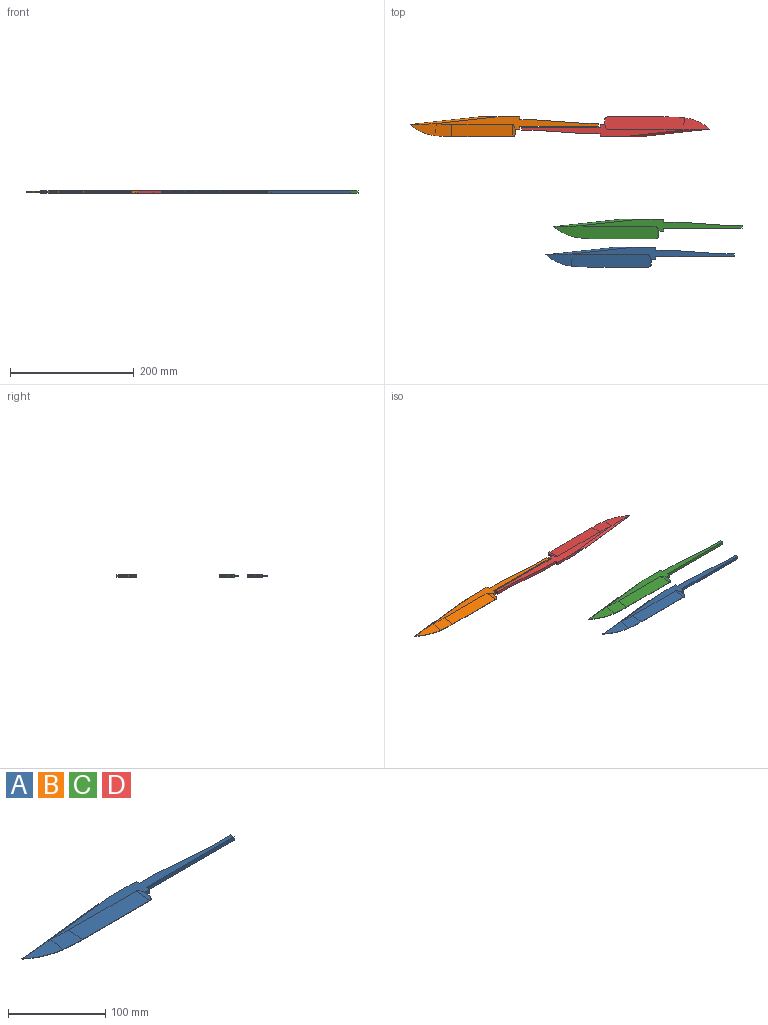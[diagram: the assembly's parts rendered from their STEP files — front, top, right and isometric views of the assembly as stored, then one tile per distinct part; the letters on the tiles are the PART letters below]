
ASSEMBLY  parts=4 mates=4
PART A: 27 faces, bbox 304.8x34.4x6.4 mm
  f0: cylinder r=4.65mm len=4.65mm, axis (0,0,-1), area 13.3mm2, adj f1,f4,f22,f26
  f1: plane 7.48x4.76mm, normal (1,0,0), area 29.5mm2, adj f0,f12,f22,f26
  f2: cylinder r=76.2mm len=40.9mm, axis (0,0,-1), area 23mm2, adj f3,f11,f17,f18,f21,f25
  f3: cylinder r=228.6mm len=26.84mm, axis (0,0,-1), area 13.7mm2, adj f2,f4,f20,f24
  f4: plane 97.93x0.51mm, normal (0,-1,0), area 49.7mm2, adj f0,f3,f19,f23
  f5: plane 4.76x4.76mm, normal (1,0,0), area 22.7mm2, adj f6,f14,f15,f16
  f6: plane 25.4x4.76mm, normal (0,1,0), area 121mm2, adj f5,f7,f15,f16
  f7: plane 76.2x5.4mm, normal (0.07,1,0), area 363.8mm2, adj f6,f8,f15,f16
  f8: plane 25.4x4.76mm, normal (0,1,0), area 121mm2, adj f7,f9,f15,f16
  f9: plane 4.76x4.73mm, normal (1,0,0), area 22.5mm2, adj f8,f10,f15,f16
  f10: plane 67.74x4.76mm, normal (0,1,0), area 257.3mm2, adj f9,f11,f15,f16,f17,f18
  f11: plane 110.06x12.13mm, normal (-0.11,0.99,0), area 28.1mm2, adj f2,f10,f17,f18
  f12: plane 7.48x4.76mm, normal (0,-1,0), area 35.6mm2, adj f1,f13,f15,f16
  f13: plane 4.76x4.73mm, normal (1,0,0), area 22.5mm2, adj f12,f14,f15,f16
  f14: plane 127x4.76mm, normal (0,-1,0), area 604.8mm2, adj f5,f13,f15,f16
  f15: plane 262.12x19.62mm, normal (0,0,1), area 2129.7mm2, adj f5,f6,f7,f8,f9,f10,f12,f13
  f16: plane 262.12x19.62mm, normal (0,0,-1), area 2129.7mm2, adj f5,f6,f7,f8,f9,f10,f12,f13
  f17: plane 139.05x12.29mm, normal (-0.06,0.58,-0.82), area 421.5mm2, adj f2,f10,f11,f16,f25
  f18: plane 139.05x12.29mm, normal (-0.06,0.58,0.82), area 421.5mm2, adj f2,f10,f11,f15,f21
  f19: plane 97.93x19.62mm, normal (0,-0.11,0.99), area 1932.8mm2, adj f4,f15,f20,f22
  f20: cone r=208.98mm half-angle=83.8deg, axis (0,0,-1), area 508.1mm2, adj f3,f15,f19,f21
  f21: cone r=56.58mm half-angle=83.8deg, axis (0,0,-1), area 510.4mm2, adj f2,f15,f18,f20
  f22: cylinder r=13.8mm len=19.71mm, axis (0,-0.99,-0.11), area 76.8mm2, adj f0,f1,f15,f19
  f23: plane 97.93x19.62mm, normal (0,-0.11,-0.99), area 1932.8mm2, adj f4,f16,f24,f26
  f24: cone r=208.98mm half-angle=83.8deg, axis (0,0,1), area 508.1mm2, adj f3,f16,f23,f25
  f25: cone r=56.58mm half-angle=83.8deg, axis (0,0,1), area 510.4mm2, adj f2,f16,f17,f24
  f26: cylinder r=13.8mm len=19.71mm, axis (0,-0.99,0.11), area 76.8mm2, adj f0,f1,f16,f23
PART B: same geometry as A
PART C: same geometry as A
PART D: same geometry as A
PLACE A t=(224.03,-196.99,-11.85)mm
PLACE B t=(3.99,13.98,-11.85)mm fixed
PLACE C t=(236.39,-151.35,-11.85)mm
PLACE D rot(axis=(0,0,1),180deg) t=(133.65,-17.77,-11.85)mm
MATE planar D.f4 <-> B.f10  axis (0,1,0) through (194.74,13.98,-11.85)mm
MATE planar B.f16 <-> C.f16  axis (0,0,-1) through (1.12,4.9,-14.23)mm
MATE planar D.f16 <-> A.f16  axis (0,0,-1) through (136.52,-8.69,-14.23)mm
MATE planar A.f16 <-> C.f16  axis (0,0,-1) through (221.16,-206.07,-14.23)mm
